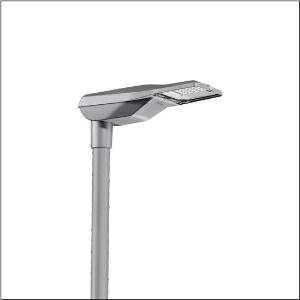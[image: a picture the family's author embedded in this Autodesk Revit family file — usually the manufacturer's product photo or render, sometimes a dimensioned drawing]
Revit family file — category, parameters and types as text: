
# Revit family: streetlight_sl_21_iq_micro___stw1_0a_5xe1e31g08db_041b
name_source: partatom
category: Lighting Fixtures
units: mm (PartAtom-declared; Revit-internal decimal feet)

## family parameters
Cut with Voids When Loaded = No
Host = Face
Light Source = No
Part Type = Normal
Room Calculation Point = No
Round Connector Dimension = Use Diameter
Shared = No

## types (1)
- --- (1 x LED, 4810 lm, 36.4 W, 3000K)
    Apparent Load = 36 VA
    CIE Flux Codes = 38 75 98 100 100
    Color Rendering = 70
    Color Temperature = 3000K
    Default Elevation = 1800 mm
    Description = Streetlight SL 21 iQ micro, mast luminaire, primary light control with lens, of PMMA, primary optical cover: cover, of toughened safety glass, transparent, light distribution: STW1.0a, light emission: direct distribution, primary light characteristic: asymmetric, installation type: post-top, side-entry, LED, High Power LED, rated luminous flux: 4.810lm, luminous efficacy: 132lm/W, light colour: 730, colour temperature: 3000K, control: Street-Remote, Auto-Match, Temp-Guard, Lumen-Switch, Night-Set, Smart-Wire, Light-Fading, Desk-Remote (wireless, voltage-free reading and setting of iQ features in the workshop via application-optimized NFC function/RFID function), optimised constant luminous flux control (CLO 2.0), presetting dimming linear, mains connection: 220..240V, AC, 50/60Hz, start of lifetime: 36W, end of service life: 38W, reduction: 16W, luminaire housing, of diecast aluminium, powder-coated, Siteco® metallic grey (DB 702S), corrosivity category C5 mid according to DIN EN ISO 12944, please order mast flange separately, inclination adjustable: 0°, 5°, 10°, 15°, sealing non-destructively replaceable, multi-level sealing system, length: 528mm, width: 235mm, height: 110mm, mast flange for spigot size: 42mm (side-entry): 5XC10008XM4, 60/48mm (side-entry/post-top): 5XC10108XM2, 76/60mm (side-entry/post-top): 5XC10108XM1, protection rating (complete): IP66, insulation class (complete): insulation class II (safety insulation), certification: CE, ENEC, ENEC+, VDE, impact resistance: IK09, permissible operating ambient temperature for outdoor applications: -40..+50°C, standard-compliant lighting for roads and squares, packaging unit: 1 piece

Light Distribution: STW1.0a
    Height = 110 mm
    Lamp = 1 x LED
    Lamp Light Flux = 4810 lm
    Lamp Power = 36.4 W
    Lamp count = 1
    Length = 528 mm
    Luminous efficacy = 132 lm/W
    Manufacturer = Siteco
    ModVariant = No
    Model = 5XE1E31G08DB
    Number of Poles = 1
    OnlyDefault = Yes
    Power Factor = 1
    Product Name = Streetlight SL 21 iQ micro | STW1.0a
    Product group = mast luminaire | pylon top
    ProductGroupID = 6100
    Protection Class = Protection class II
    Protection Degree = IP 66
    RLX_Detail_Level = 1
    RLX_Emergency_Light_Flux = 0 lm
    RLX_Emergency_Type = 0
    RLX_Emergency_Type_DB = No
    RlxData = <blob elided: 99301 chars, md5=15e80d4b>
    Socket = socket
    Standby Power = 0 W
    System Light Flux = 4810 lm
    System Power = 36 W
    Type Comments = factory setting: luminous flux: 100 % | dim-lin: 254 | 715 mA
    Type Image = l_1006881.jpg
    URL = http://relux.com
    VarID = @adj_105617
    Voltage = 0 V
    Weight = 0.00 kg
    Width = 235 mm

## geometry (parser evidence)
native form markers: Blend x4, Sweep x10
no freeform markers — native parametric forms only
